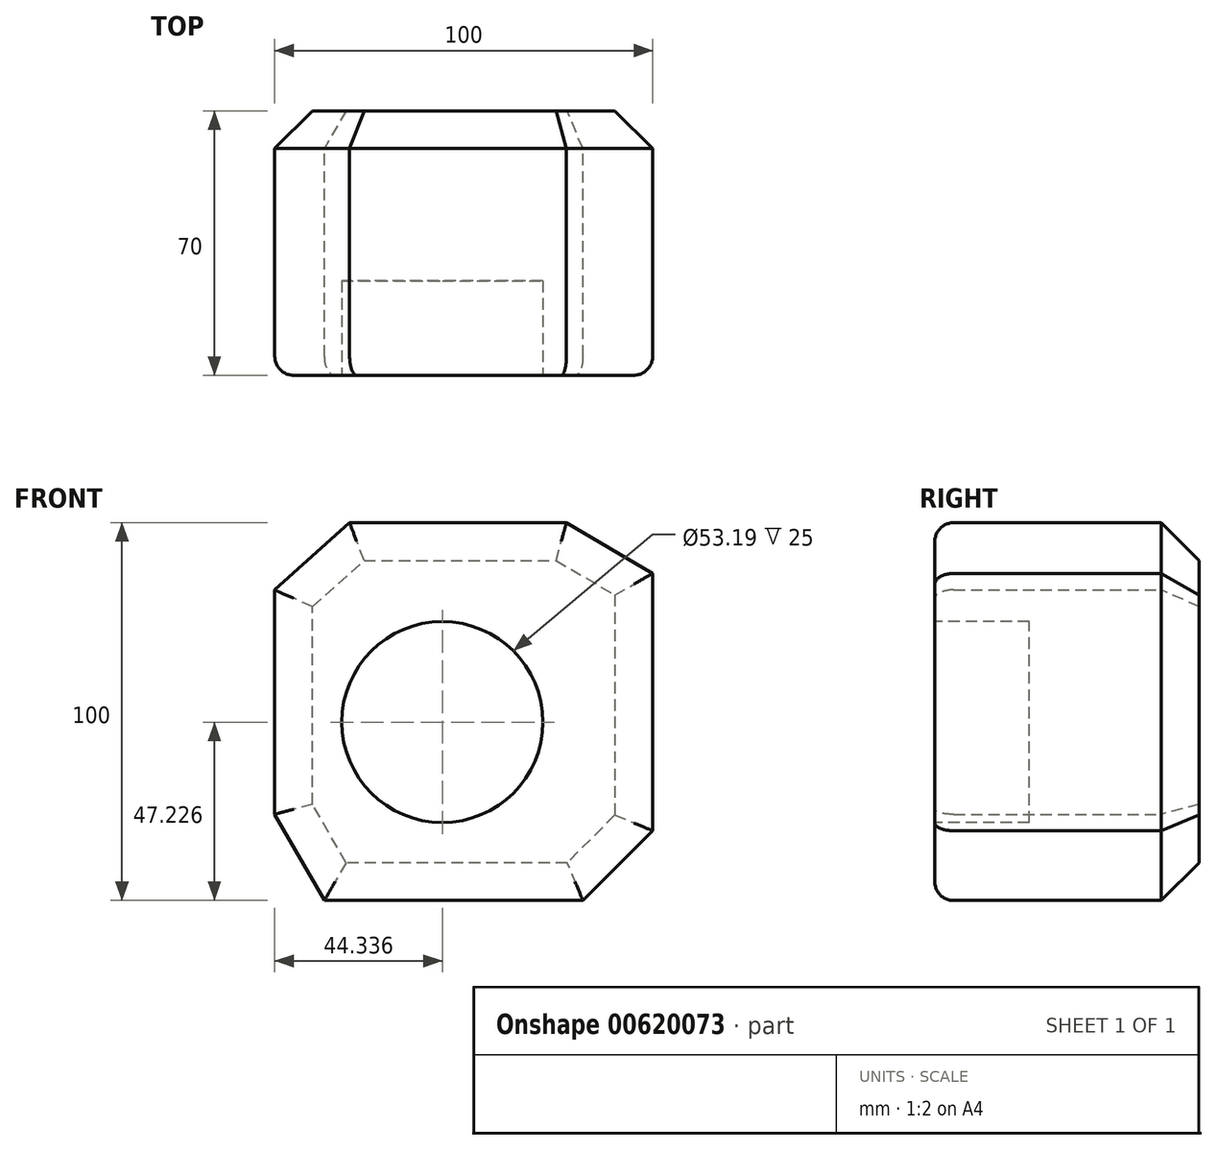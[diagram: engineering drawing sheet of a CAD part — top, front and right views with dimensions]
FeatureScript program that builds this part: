
annotation { "Feature Type Name" : "Feature", "Feature Type Description" : "" }
export const myFeature = defineFeature(function(context is Context, id is Id, definition is map)
    precondition{}
    {
        {
            var Q0;
            Q0=qCreatedBy(makeId("Front.planeOp"),FACE);
            var sketch = newSketch(context, id + "F0", { "sketchPlane" : qUnion([Q0])});
            skLineSegment(sketch, "E0.bottom", {"start": v(-34.37, 48.43) * mm, "end": v(23, 48.43) * mm});
            skLineSegment(sketch, "E0.top", {"start": v(-41.08, -51.57) * mm, "end": v(27.37, -51.57) * mm});
            skLineSegment(sketch, "E0.left", {"start": v(-54.16, 30.63) * mm, "end": v(-54.16, -28.76) * mm});
            skLineSegment(sketch, "E0.right", {"start": v(45.84, 35) * mm, "end": v(45.84, -33.12) * mm});
            skLineSegment(sketch, "E1", {"start": v(-34.37, 48.43) * mm, "end": v(-54.16, 30.63) * mm});
            skLineSegment(sketch, "E2", {"start": v(45.84, -33.12) * mm, "end": v(27.37, -51.57) * mm});
            skLineSegment(sketch, "E3", {"start": v(-54.16, -28.76) * mm, "end": v(-41.08, -51.57) * mm});
            skLineSegment(sketch, "E4", {"start": v(23, 48.43) * mm, "end": v(45.84, 35) * mm});
            skSolve(sketch);
        }
        {
            var Q0;
            Q0 = qSketchRegion(id + "F0", true);
            extrude(context, id + "F1", {"entities" : qUnion([Q0]), "depth" : 70 * mm, "offsetDistance" : 25 * mm});
        }
        {
            var Q0;
            Q0=makeQuery(id+"F1.opExtrude","CAP_FACE",FACE,{"disambiguationData":[OSD([sQuery(id+"F0.wireOp",EDGE,"E0.bottom"),sQuery(id+"F0.wireOp",EDGE,"E0.top"),sQuery(id+"F0.wireOp",EDGE,"E0.left"),sQuery(id+"F0.wireOp",EDGE,"E0.right"),sQuery(id+"F0.wireOp",EDGE,"E1"),sQuery(id+"F0.wireOp",EDGE,"E2"),sQuery(id+"F0.wireOp",EDGE,"E3"),sQuery(id+"F0.wireOp",EDGE,"E4")])],"isStart":true});
            chamfer(context, id + "F2", {"entities" : qUnion([Q0]), "width" : 10 * mm, "tangentPropagation" : true});
        }
        {
            var Q0;
            Q0=makeQuery(id+"F1.opExtrude","CAP_FACE",FACE,{"disambiguationData":[OSD([sQuery(id+"F0.wireOp",EDGE,"E0.bottom"),sQuery(id+"F0.wireOp",EDGE,"E0.top"),sQuery(id+"F0.wireOp",EDGE,"E0.left"),sQuery(id+"F0.wireOp",EDGE,"E0.right"),sQuery(id+"F0.wireOp",EDGE,"E1"),sQuery(id+"F0.wireOp",EDGE,"E2"),sQuery(id+"F0.wireOp",EDGE,"E3"),sQuery(id+"F0.wireOp",EDGE,"E4")])],"isStart":false});
            fillet(context, id + "F3", {"entities" : qUnion([Q0]), "radius" : 5 * mm, "tangentPropagation" : true, "allowEdgeOverflow" : false});
        }
        {
            var Q0;
            Q0=makeQuery(id+"F1.opExtrude","CAP_FACE",FACE,{"disambiguationData":[OSD([sQuery(id+"F0.wireOp",EDGE,"E0.bottom"),sQuery(id+"F0.wireOp",EDGE,"E0.top"),sQuery(id+"F0.wireOp",EDGE,"E0.left"),sQuery(id+"F0.wireOp",EDGE,"E0.right"),sQuery(id+"F0.wireOp",EDGE,"E1"),sQuery(id+"F0.wireOp",EDGE,"E2"),sQuery(id+"F0.wireOp",EDGE,"E3"),sQuery(id+"F0.wireOp",EDGE,"E4")])],"isStart":true});
            var sketch = newSketch(context, id + "F4", { "sketchPlane" : qUnion([Q0])});
            skCircle(sketch, "E5", {"center": v(0, 0) * mm, "radius": 21.5 * mm});
            skSolve(sketch);
        }
        {
            var Q0;
            Q0=makeQuery(id+"F4.imprint","IMPRINT",FACE,{"disambiguationData":[TD([[makeQuery(id+"F4.imprint","IMPRINT",EDGE,{"derivedFrom":sQuery(id+"F4.wireOp",EDGE,"E5")}),1.0]])]});
            extrude(context, id + "F5", {"entities" : qUnion([Q0]), "operationType" : NewBodyOperationType.ADD, "oppositeDirection" : true, "depth" : 39.1 * mm, "offsetDistance" : 25 * mm});
        }
        {
            var Q0;
            Q0=makeQuery(id+"F1.opExtrude","CAP_FACE",FACE,{"disambiguationData":[OSD([sQuery(id+"F0.wireOp",EDGE,"E0.bottom"),sQuery(id+"F0.wireOp",EDGE,"E0.top"),sQuery(id+"F0.wireOp",EDGE,"E0.left"),sQuery(id+"F0.wireOp",EDGE,"E0.right"),sQuery(id+"F0.wireOp",EDGE,"E1"),sQuery(id+"F0.wireOp",EDGE,"E2"),sQuery(id+"F0.wireOp",EDGE,"E3"),sQuery(id+"F0.wireOp",EDGE,"E4")])],"isStart":false});
            var sketch = newSketch(context, id + "F6", { "sketchPlane" : qUnion([Q0])});
            skCircle(sketch, "E6", {"center": v(-9.82, -4.34) * mm, "radius": 26.6 * mm});
            skSolve(sketch);
        }
        {
            var Q0;
            Q0=makeQuery(id+"F6.imprint","IMPRINT",FACE,{"disambiguationData":[TD([[makeQuery(id+"F6.imprint","IMPRINT",EDGE,{"derivedFrom":sQuery(id+"F6.wireOp",EDGE,"E6")}),1.0]])]});
            extrude(context, id + "F7", {"entities" : qUnion([Q0]), "operationType" : NewBodyOperationType.REMOVE, "oppositeDirection" : true, "depth" : 25 * mm, "offsetDistance" : 25 * mm});
        }
    });
